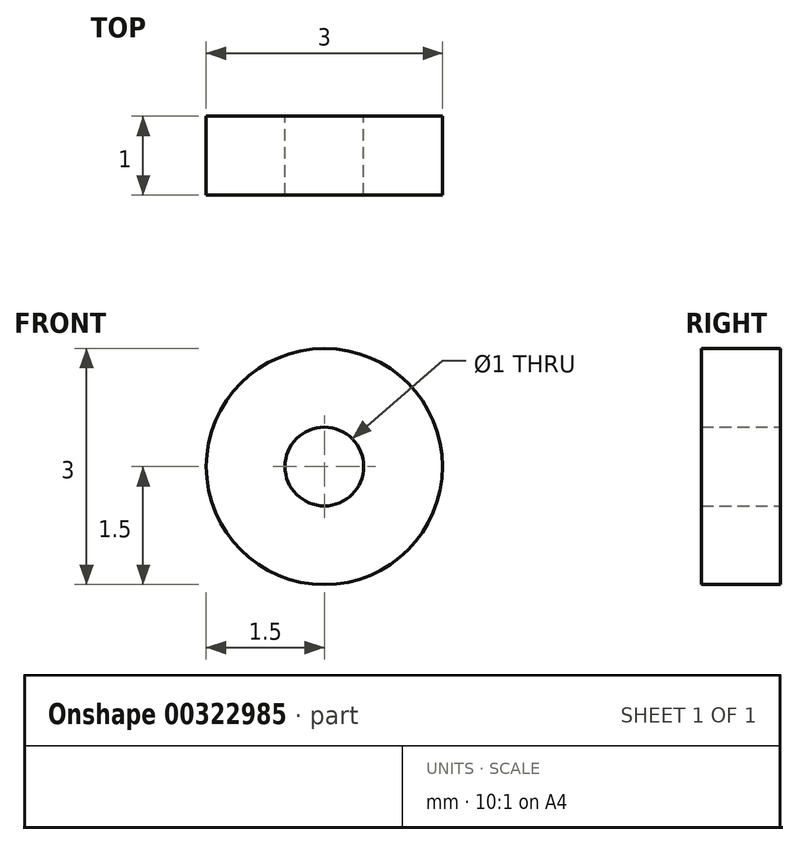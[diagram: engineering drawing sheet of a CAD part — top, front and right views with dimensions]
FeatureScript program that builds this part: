
annotation { "Feature Type Name" : "Feature", "Feature Type Description" : "" }
export const myFeature = defineFeature(function(context is Context, id is Id, definition is map)
    precondition{}
    {
        {
            var Q0;
            Q0=qCreatedBy(makeId("Front.planeOp"),FACE);
            var sketch = newSketch(context, id + "F0", { "sketchPlane" : qUnion([Q0])});
            skCircle(sketch, "E0", {"center": v(0, 0) * mm, "radius": 0.5 * mm});
            skCircle(sketch, "E1", {"center": v(0, 0) * mm, "radius": 1.5 * mm});
            skSolve(sketch);
        }
        {
            var Q0;
            Q0 = qSketchRegion(id + "F0", true);
            extrude(context, id + "F1", {"entities" : qUnion([Q0]), "depth" : 1 * mm});
        }
    });
